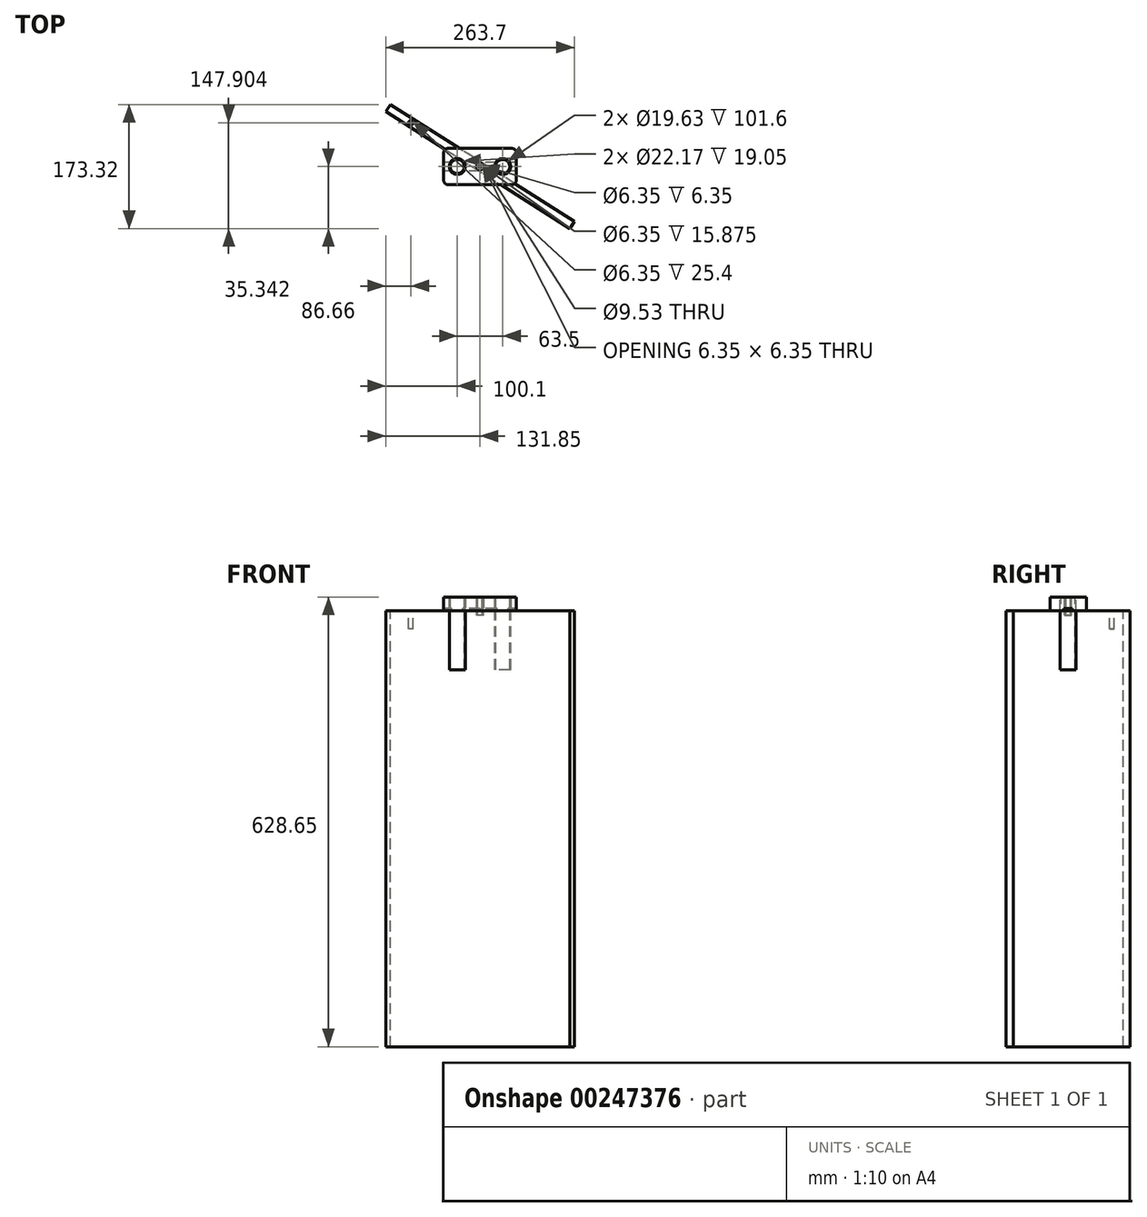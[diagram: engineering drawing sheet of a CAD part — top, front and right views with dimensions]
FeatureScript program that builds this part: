
annotation { "Feature Type Name" : "Feature", "Feature Type Description" : "" }
export const myFeature = defineFeature(function(context is Context, id is Id, definition is map)
    precondition{}
    {
        {
            var Q0;
            Q0=qCreatedBy(makeId("Top.planeOp"),FACE);
            var sketch = newSketch(context, id + "F0", { "sketchPlane" : qUnion([Q0])});
            skLineSegment(sketch, "E0.bottom", {"start": v(50.8, -25.4) * mm, "end": v(-50.8, -25.4) * mm});
            skLineSegment(sketch, "E0.top", {"start": v(50.8, 25.4) * mm, "end": v(-50.8, 25.4) * mm});
            skLineSegment(sketch, "E0.left", {"start": v(50.8, -25.4) * mm, "end": v(50.8, 25.4) * mm});
            skLineSegment(sketch, "E0.right", {"start": v(-50.8, -25.4) * mm, "end": v(-50.8, 25.4) * mm});
            skPoint(sketch, "E0.middle", {"position": v(0, 0) * mm});
            skCircle(sketch, "E1", {"center": v(-31.75, 0) * mm, "radius": 11.09 * mm});
            skCircle(sketch, "E2", {"center": v(31.75, 0) * mm, "radius": 11.09 * mm});
            skCircle(sketch, "E3", {"center": v(0, 0) * mm, "radius": 4.76 * mm});
            skSolve(sketch);
        }
        {
            var Q0;
            Q0 = qSketchRegion(id + "F0", true);
            extrude(context, id + "F1", {"entities" : qUnion([Q0]), "depth" : 19.05 * mm});
        }
        {
            var Q0;
            Q0=makeQuery(id+"F1.opExtrude","CAP_FACE",FACE,{"disambiguationData":[OSD([sQuery(id+"F0.wireOp",EDGE,"E0.bottom"),sQuery(id+"F0.wireOp",EDGE,"E0.top"),sQuery(id+"F0.wireOp",EDGE,"E0.left"),sQuery(id+"F0.wireOp",EDGE,"E0.right"),sQuery(id+"F0.wireOp",EDGE,"E1"),sQuery(id+"F0.wireOp",EDGE,"E2"),sQuery(id+"F0.wireOp",EDGE,"E3")])],"isStart":false});
            var sketch = newSketch(context, id + "F2", { "sketchPlane" : qUnion([Q0])});
            skCircle(sketch, "E4.0", {"center": v(-31.75, 0) * mm, "radius": 11.09 * mm});
            skCircle(sketch, "E5.0", {"center": v(-31.75, 0) * mm, "radius": 9.82 * mm});
            skCircle(sketch, "E6.0", {"center": v(31.75, 0) * mm, "radius": 11.09 * mm});
            skCircle(sketch, "E7.0", {"center": v(31.75, 0) * mm, "radius": 9.82 * mm});
            skSolve(sketch);
        }
        {
            var Q0;
            Q0 = qSketchRegion(id + "F2", true);
            extrude(context, id + "F3", {"entities" : qUnion([Q0]), "oppositeDirection" : true, "depth" : 101.6 * mm});
        }
        {
            var Q0;
            Q0=makeQuery(id+"F1.opExtrude","CAP_FACE",FACE,{"disambiguationData":[OSD([sQuery(id+"F0.wireOp",EDGE,"E0.bottom"),sQuery(id+"F0.wireOp",EDGE,"E0.top"),sQuery(id+"F0.wireOp",EDGE,"E0.left"),sQuery(id+"F0.wireOp",EDGE,"E0.right"),sQuery(id+"F0.wireOp",EDGE,"E1"),sQuery(id+"F0.wireOp",EDGE,"E2"),sQuery(id+"F0.wireOp",EDGE,"E3")])],"isStart":false});
            var sketch = newSketch(context, id + "F4", { "sketchPlane" : qUnion([Q0])});
            skCircle(sketch, "E8.0", {"center": v(0, 0) * mm, "radius": 4.76 * mm});
            skCircle(sketch, "E9", {"center": v(0, 0) * mm, "radius": 3.17 * mm});
            skSolve(sketch);
        }
        {
            var Q0;
            Q0 = qSketchRegion(id + "F4", true);
            extrude(context, id + "F5", {"entities" : qUnion([Q0]), "oppositeDirection" : true, "depth" : 25.4 * mm});
        }
        {
            var Q0;
            Q0=makeQuery(id+"F1.opExtrude","SWEPT_EDGE",EDGE,{"disambiguationData":[OSD([sQuery(id+"F0.wireOp",EDGE,"E0.bottom"),sQuery(id+"F0.wireOp",EDGE,"E0.right")])]});
            var Q1;
            Q1=makeQuery(id+"F1.opExtrude","SWEPT_EDGE",EDGE,{"disambiguationData":[OSD([sQuery(id+"F0.wireOp",EDGE,"E0.top"),sQuery(id+"F0.wireOp",EDGE,"E0.right")])]});
            var Q2;
            Q2=makeQuery(id+"F1.opExtrude","SWEPT_EDGE",EDGE,{"disambiguationData":[OSD([sQuery(id+"F0.wireOp",EDGE,"E0.bottom"),sQuery(id+"F0.wireOp",EDGE,"E0.left")])]});
            var Q3;
            Q3=makeQuery(id+"F1.opExtrude","SWEPT_EDGE",EDGE,{"disambiguationData":[OSD([sQuery(id+"F0.wireOp",EDGE,"E0.top"),sQuery(id+"F0.wireOp",EDGE,"E0.left")])]});
            fillet(context, id + "F6", {"entities" : qUnion([Q0, Q1, Q2, Q3]), "radius" : 6.35 * mm, "tangentPropagation" : true, "allowEdgeOverflow" : false});
        }
        {
            var Q0;
            Q0=makeQuery(id+"F1.opExtrude","CAP_FACE",FACE,{"disambiguationData":[OSD([sQuery(id+"F0.wireOp",EDGE,"E0.bottom"),sQuery(id+"F0.wireOp",EDGE,"E0.top"),sQuery(id+"F0.wireOp",EDGE,"E0.left"),sQuery(id+"F0.wireOp",EDGE,"E0.right"),sQuery(id+"F0.wireOp",EDGE,"E1"),sQuery(id+"F0.wireOp",EDGE,"E2"),sQuery(id+"F0.wireOp",EDGE,"E3")])],"isStart":true});
            var sketch = newSketch(context, id + "F7", { "sketchPlane" : qUnion([Q0])});
            skLineSegment(sketch, "E10", {"start": v(-131.85, -76.66) * mm, "end": v(125.5, 86.66) * mm});
            skLineSegment(sketch, "E11", {"start": v(125.5, 86.66) * mm, "end": v(131.85, 76.66) * mm});
            skLineSegment(sketch, "E12", {"start": v(131.85, 76.66) * mm, "end": v(-125.5, -86.66) * mm});
            skLineSegment(sketch, "E13", {"start": v(-125.5, -86.66) * mm, "end": v(-131.85, -76.66) * mm});
            skLineSegment(sketch, "E14", {"start": v(-3.17, 5) * mm, "end": v(3.17, -5) * mm, "construction": true});
            skSolve(sketch);
        }
        {
            var Q0;
            Q0 = qSketchRegion(id + "F7", true);
            extrude(context, id + "F8", {"entities" : qUnion([Q0]), "depth" : 609.6 * mm});
        }
        {
            var Q0;
            Q0=makeQuery(id+"F8.opExtrude","CAP_FACE",FACE,{"disambiguationData":[OSD([sQuery(id+"F7.wireOp",EDGE,"E10"),sQuery(id+"F7.wireOp",EDGE,"E11"),sQuery(id+"F7.wireOp",EDGE,"E12"),sQuery(id+"F7.wireOp",EDGE,"E13")])],"isStart":true});
            var sketch = newSketch(context, id + "F9", { "sketchPlane" : qUnion([Q0])});
            skLineSegment(sketch, "E15", {"start": v(-128.68, 81.66) * mm, "end": v(-96.5, 61.24) * mm, "construction": true});
            skCircle(sketch, "E16", {"center": v(-96.5, 61.24) * mm, "radius": 3.18 * mm});
            skSolve(sketch);
        }
        {
            var Q0;
            Q0 = qSketchRegion(id + "F9", true);
            extrude(context, id + "F10", {"entities" : qUnion([Q0]), "operationType" : NewBodyOperationType.REMOVE, "oppositeDirection" : true, "depth" : 25.4 * mm});
        }
        {
            var Q0;
            Q0=makeQuery(id+"F1.opExtrude","CAP_FACE",FACE,{"disambiguationData":[OSD([sQuery(id+"F0.wireOp",EDGE,"E0.bottom"),sQuery(id+"F0.wireOp",EDGE,"E0.top"),sQuery(id+"F0.wireOp",EDGE,"E0.left"),sQuery(id+"F0.wireOp",EDGE,"E0.right"),sQuery(id+"F0.wireOp",EDGE,"E1"),sQuery(id+"F0.wireOp",EDGE,"E2"),sQuery(id+"F0.wireOp",EDGE,"E3")])],"isStart":true});
            var sketch = newSketch(context, id + "F11", { "sketchPlane" : qUnion([Q0])});
            skLineSegment(sketch, "E17.bottom", {"start": v(50.8, -6) * mm, "end": v(-50.8, -6) * mm});
            skLineSegment(sketch, "E17.top", {"start": v(50.8, 6) * mm, "end": v(-50.8, 6) * mm});
            skLineSegment(sketch, "E17.left", {"start": v(50.8, -6) * mm, "end": v(50.8, 6) * mm});
            skLineSegment(sketch, "E17.right", {"start": v(-50.8, -6) * mm, "end": v(-50.8, 6) * mm});
            skPoint(sketch, "E17.middle", {"position": v(0, 0) * mm});
            skSolve(sketch);
        }
        {
            var Q0;
            Q0 = qSketchRegion(id + "F11", true);
            extrude(context, id + "F12", {"entities" : qUnion([Q0]), "operationType" : NewBodyOperationType.REMOVE, "oppositeDirection" : true, "depth" : 3.17 * mm});
        }
    });
